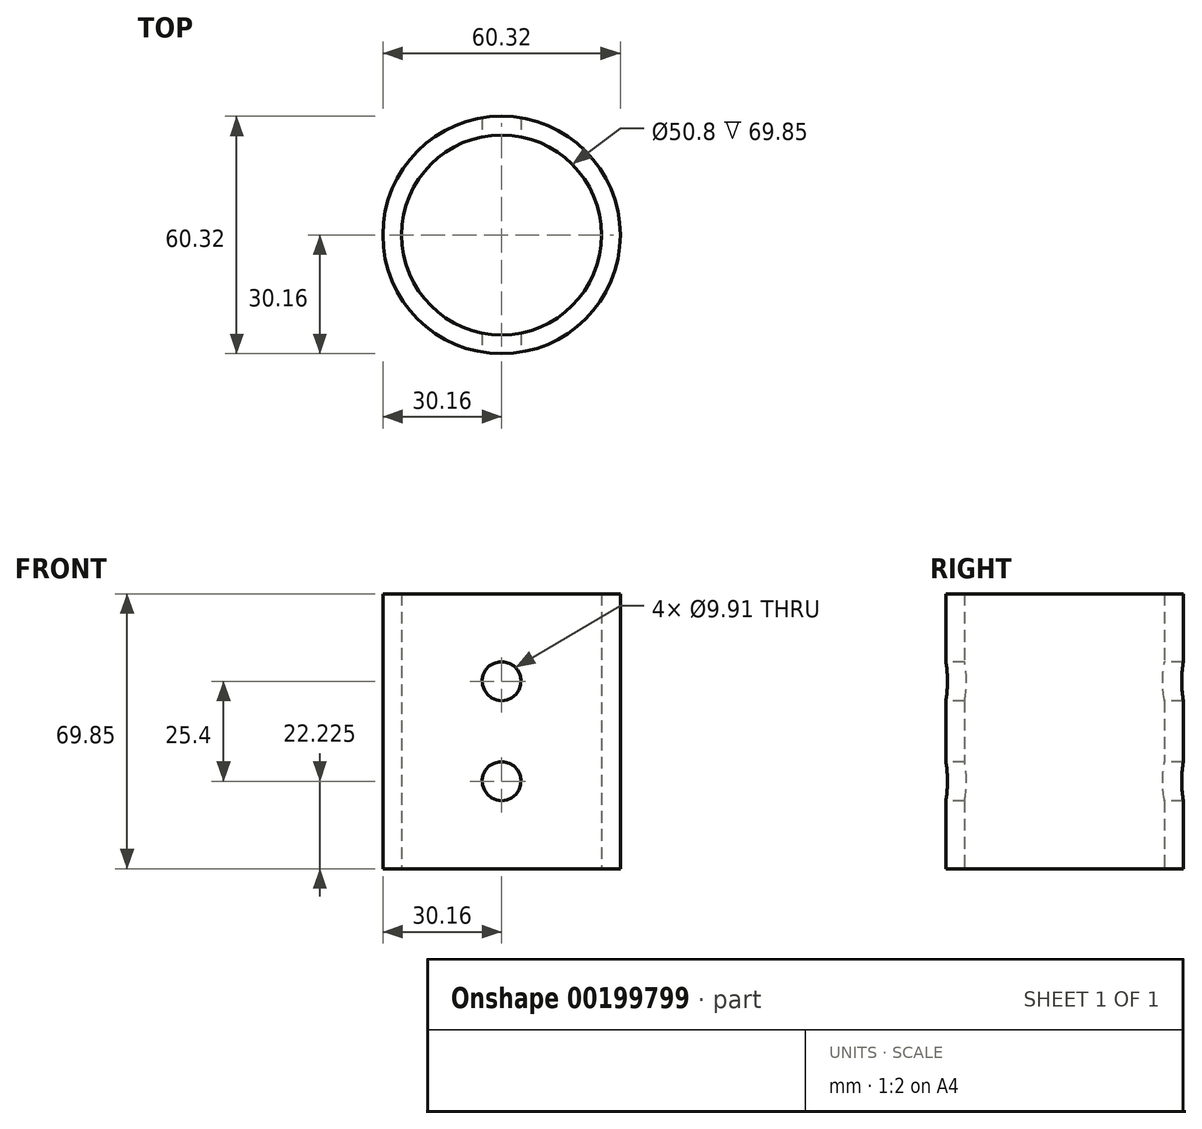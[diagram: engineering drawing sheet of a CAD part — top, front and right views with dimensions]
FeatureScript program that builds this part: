
annotation { "Feature Type Name" : "Feature", "Feature Type Description" : "" }
export const myFeature = defineFeature(function(context is Context, id is Id, definition is map)
    precondition{}
    {
        {
            var Q0;
            Q0=qCreatedBy(makeId("Top.planeOp"),FACE);
            var sketch = newSketch(context, id + "F0", { "sketchPlane" : qUnion([Q0])});
            skCircle(sketch, "E0", {"center": v(0, 0) * mm, "radius": 30.16 * mm});
            skCircle(sketch, "E1", {"center": v(0, 0) * mm, "radius": 25.4 * mm});
            skSolve(sketch);
        }
        {
            var Q0;
            Q0 = qSketchRegion(id + "F0", true);
            extrude(context, id + "F1", {"entities" : qUnion([Q0]), "depth" : 69.85 * mm});
        }
        {
            var Q0;
            Q0=qCreatedBy(makeId("Front.planeOp"),FACE);
            var sketch = newSketch(context, id + "F2", { "sketchPlane" : qUnion([Q0])});
            skCircle(sketch, "E2", {"center": v(0, 47.63) * mm, "radius": 4.95 * mm});
            skCircle(sketch, "E3", {"center": v(0, 22.23) * mm, "radius": 4.95 * mm});
            skSolve(sketch);
        }
        {
            var Q0;
            Q0 = qSketchRegion(id + "F2", true);
            extrude(context, id + "F3", {"entities" : qUnion([Q0]), "operationType" : NewBodyOperationType.REMOVE, "endBound" : BoundingType.SYMMETRIC, "oppositeDirection" : true, "depth" : 63.5 * mm});
        }
    });
